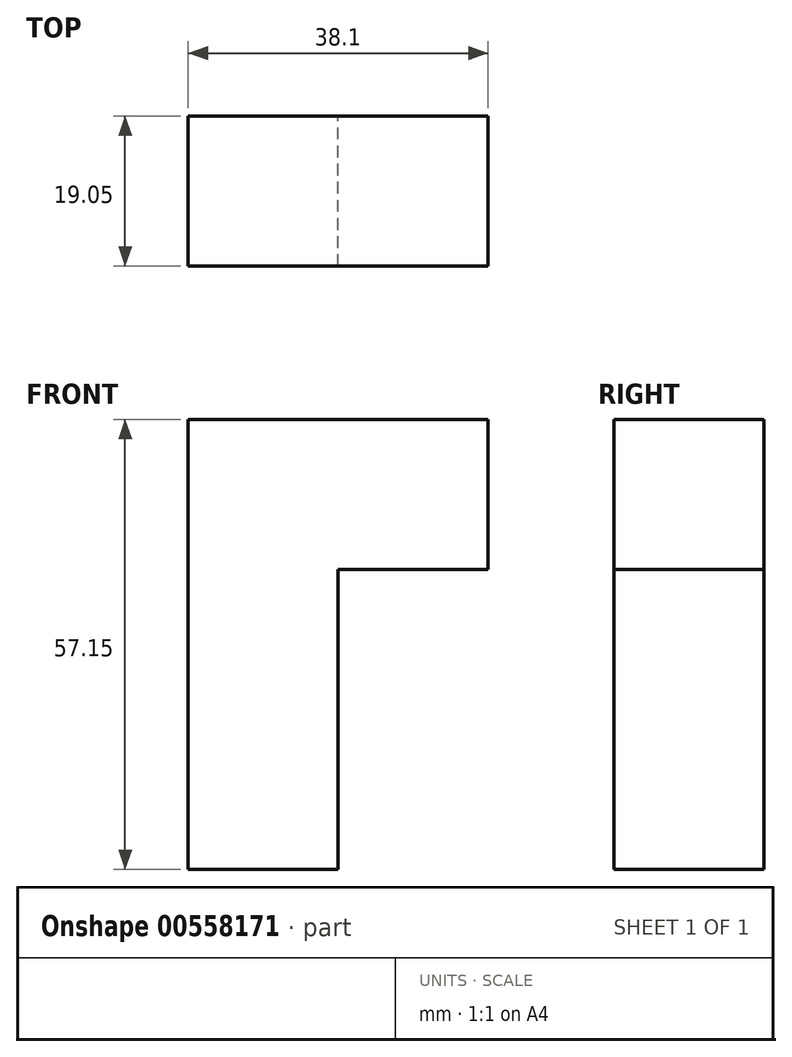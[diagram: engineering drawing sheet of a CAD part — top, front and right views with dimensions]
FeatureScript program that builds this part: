
annotation { "Feature Type Name" : "Feature", "Feature Type Description" : "" }
export const myFeature = defineFeature(function(context is Context, id is Id, definition is map)
    precondition{}
    {
        {
            var Q0;
            Q0=qCreatedBy(makeId("Front.planeOp"),FACE);
            var sketch = newSketch(context, id + "F0", { "sketchPlane" : qUnion([Q0])});
            skLineSegment(sketch, "E0", {"start": v(0, 0) * mm, "end": v(0, -57.15) * mm});
            skLineSegment(sketch, "E1", {"start": v(0, 0) * mm, "end": v(38.1, 0) * mm});
            skLineSegment(sketch, "E2", {"start": v(38.1, 0) * mm, "end": v(38.1, -19.05) * mm});
            skLineSegment(sketch, "E3", {"start": v(38.1, -19.05) * mm, "end": v(19.05, -19.05) * mm});
            skLineSegment(sketch, "E4", {"start": v(19.05, -19.05) * mm, "end": v(19.05, -57.15) * mm});
            skLineSegment(sketch, "E5", {"start": v(19.05, -57.15) * mm, "end": v(0, -57.15) * mm});
            skSolve(sketch);
        }
        {
            var Q0;
            Q0 = qSketchRegion(id + "F0", true);
            extrude(context, id + "F1", {"entities" : qUnion([Q0]), "depth" : 19.05 * mm, "offsetDistance" : 25.4 * mm});
        }
    });
